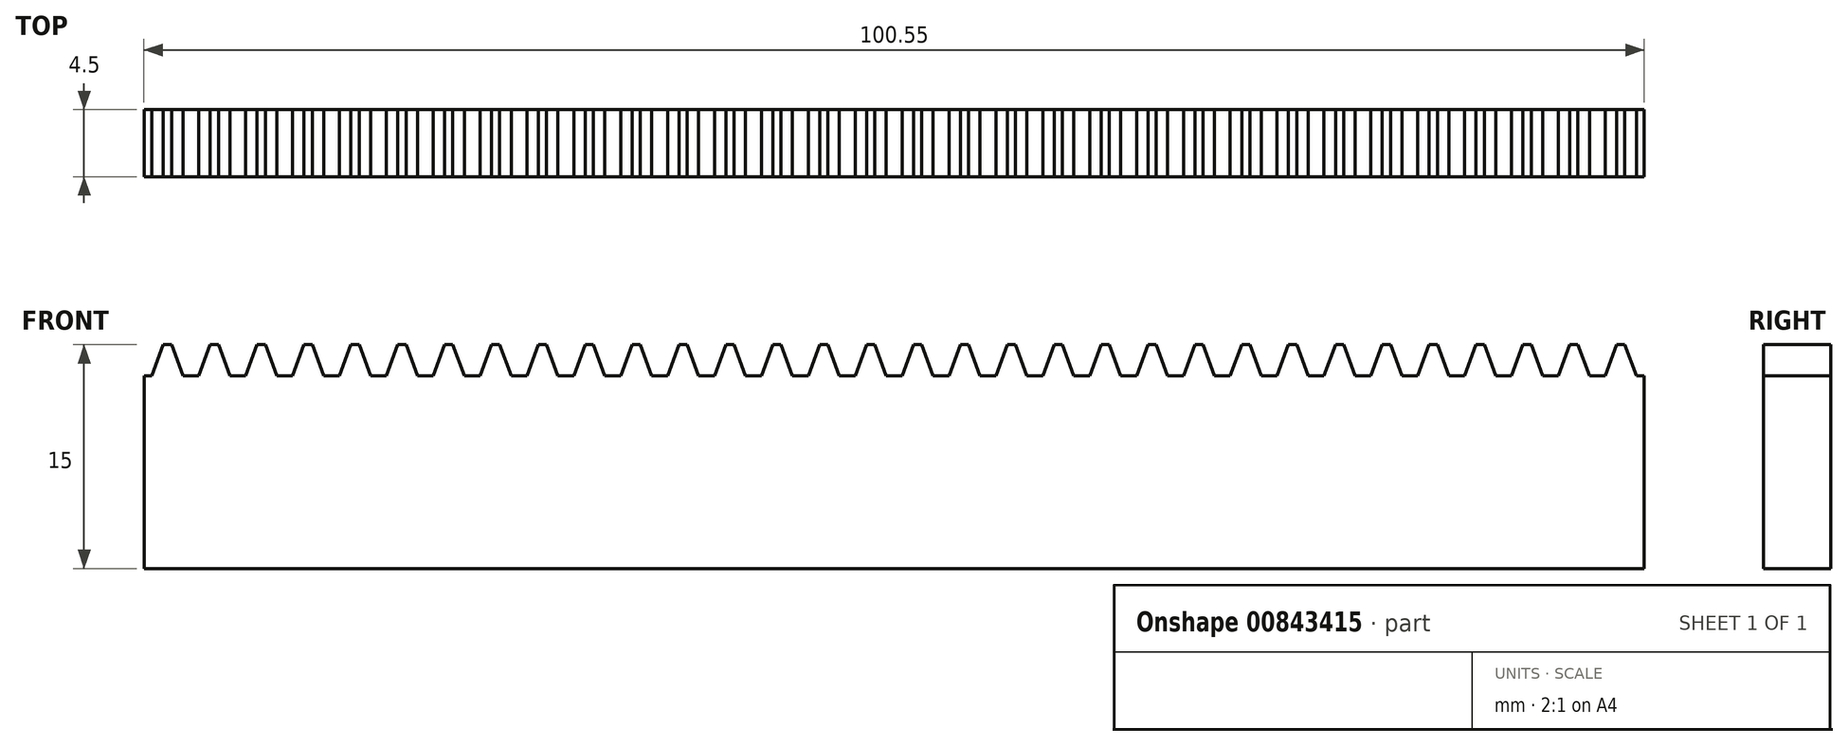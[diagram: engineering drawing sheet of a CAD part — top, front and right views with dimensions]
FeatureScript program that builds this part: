
annotation { "Feature Type Name" : "Feature", "Feature Type Description" : "" }
export const myFeature = defineFeature(function(context is Context, id is Id, definition is map)
    precondition{}
    {
        {
            var Q0;
            Q0=qCreatedBy(makeId("Front.planeOp"),FACE);
            var sketch = newSketch(context, id + "F0", { "sketchPlane" : qUnion([Q0])});
            skLineSegment(sketch, "E0", {"start": v(-394.15, -7.5) * mm, "end": v(-494.7, -7.5) * mm});
            skLineSegment(sketch, "E1", {"start": v(-394.15, 5.4) * mm, "end": v(-394.69, 5.4) * mm});
            skLineSegment(sketch, "E2", {"start": v(-394.69, 5.4) * mm, "end": v(-395.45, 7.5) * mm});
            skLineSegment(sketch, "E3", {"start": v(-396, 7.5) * mm, "end": v(-395.45, 7.5) * mm});
            skLineSegment(sketch, "E4", {"start": v(-396, 7.5) * mm, "end": v(-396.76, 5.4) * mm});
            skLineSegment(sketch, "E5", {"start": v(-396.76, 5.4) * mm, "end": v(-397.83, 5.4) * mm});
            skLineSegment(sketch, "E6", {"start": v(-397.83, 5.4) * mm, "end": v(-398.6, 7.5) * mm});
            skLineSegment(sketch, "E7", {"start": v(-399.14, 7.5) * mm, "end": v(-398.6, 7.5) * mm});
            skLineSegment(sketch, "E8", {"start": v(-399.14, 7.5) * mm, "end": v(-399.9, 5.4) * mm});
            skLineSegment(sketch, "E9", {"start": v(-399.9, 5.4) * mm, "end": v(-400.97, 5.4) * mm});
            skLineSegment(sketch, "E10", {"start": v(-400.97, 5.4) * mm, "end": v(-401.73, 7.5) * mm});
            skLineSegment(sketch, "E11", {"start": v(-402.28, 7.5) * mm, "end": v(-401.73, 7.5) * mm});
            skLineSegment(sketch, "E12", {"start": v(-402.28, 7.5) * mm, "end": v(-403.04, 5.4) * mm});
            skLineSegment(sketch, "E13", {"start": v(-403.04, 5.4) * mm, "end": v(-404.11, 5.4) * mm});
            skLineSegment(sketch, "E14", {"start": v(-404.11, 5.4) * mm, "end": v(-404.88, 7.5) * mm});
            skLineSegment(sketch, "E15", {"start": v(-405.42, 7.5) * mm, "end": v(-404.88, 7.5) * mm});
            skLineSegment(sketch, "E16", {"start": v(-405.42, 7.5) * mm, "end": v(-406.19, 5.4) * mm});
            skLineSegment(sketch, "E17", {"start": v(-406.19, 5.4) * mm, "end": v(-407.25, 5.4) * mm});
            skLineSegment(sketch, "E18", {"start": v(-407.25, 5.4) * mm, "end": v(-408.02, 7.5) * mm});
            skLineSegment(sketch, "E19", {"start": v(-408.56, 7.5) * mm, "end": v(-408.02, 7.5) * mm});
            skLineSegment(sketch, "E20", {"start": v(-408.56, 7.5) * mm, "end": v(-409.33, 5.4) * mm});
            skLineSegment(sketch, "E21", {"start": v(-409.33, 5.4) * mm, "end": v(-410.4, 5.4) * mm});
            skLineSegment(sketch, "E22", {"start": v(-410.4, 5.4) * mm, "end": v(-411.16, 7.5) * mm});
            skLineSegment(sketch, "E23", {"start": v(-411.7, 7.5) * mm, "end": v(-411.16, 7.5) * mm});
            skLineSegment(sketch, "E24", {"start": v(-411.7, 7.5) * mm, "end": v(-412.47, 5.4) * mm});
            skLineSegment(sketch, "E25", {"start": v(-412.47, 5.4) * mm, "end": v(-413.54, 5.4) * mm});
            skLineSegment(sketch, "E26", {"start": v(-413.54, 5.4) * mm, "end": v(-414.3, 7.5) * mm});
            skLineSegment(sketch, "E27", {"start": v(-414.85, 7.5) * mm, "end": v(-414.3, 7.5) * mm});
            skLineSegment(sketch, "E28", {"start": v(-414.85, 7.5) * mm, "end": v(-415.61, 5.4) * mm});
            skLineSegment(sketch, "E29", {"start": v(-415.61, 5.4) * mm, "end": v(-416.68, 5.4) * mm});
            skLineSegment(sketch, "E30", {"start": v(-416.68, 5.4) * mm, "end": v(-417.44, 7.5) * mm});
            skLineSegment(sketch, "E31", {"start": v(-417.99, 7.5) * mm, "end": v(-417.44, 7.5) * mm});
            skLineSegment(sketch, "E32", {"start": v(-417.99, 7.5) * mm, "end": v(-418.75, 5.4) * mm});
            skLineSegment(sketch, "E33", {"start": v(-418.75, 5.4) * mm, "end": v(-419.82, 5.4) * mm});
            skLineSegment(sketch, "E34", {"start": v(-419.82, 5.4) * mm, "end": v(-420.59, 7.5) * mm});
            skLineSegment(sketch, "E35", {"start": v(-421.13, 7.5) * mm, "end": v(-420.59, 7.5) * mm});
            skLineSegment(sketch, "E36", {"start": v(-421.13, 7.5) * mm, "end": v(-421.9, 5.4) * mm});
            skLineSegment(sketch, "E37", {"start": v(-421.9, 5.4) * mm, "end": v(-422.96, 5.4) * mm});
            skLineSegment(sketch, "E38", {"start": v(-422.96, 5.4) * mm, "end": v(-423.73, 7.5) * mm});
            skLineSegment(sketch, "E39", {"start": v(-424.27, 7.5) * mm, "end": v(-423.73, 7.5) * mm});
            skLineSegment(sketch, "E40", {"start": v(-424.27, 7.5) * mm, "end": v(-425.04, 5.4) * mm});
            skLineSegment(sketch, "E41", {"start": v(-425.04, 5.4) * mm, "end": v(-426.1, 5.4) * mm});
            skLineSegment(sketch, "E42", {"start": v(-426.1, 5.4) * mm, "end": v(-426.87, 7.5) * mm});
            skLineSegment(sketch, "E43", {"start": v(-427.42, 7.5) * mm, "end": v(-426.87, 7.5) * mm});
            skLineSegment(sketch, "E44", {"start": v(-427.42, 7.5) * mm, "end": v(-428.18, 5.4) * mm});
            skLineSegment(sketch, "E45", {"start": v(-428.18, 5.4) * mm, "end": v(-429.25, 5.4) * mm});
            skLineSegment(sketch, "E46", {"start": v(-429.25, 5.4) * mm, "end": v(-430.01, 7.5) * mm});
            skLineSegment(sketch, "E47", {"start": v(-430.56, 7.5) * mm, "end": v(-430.01, 7.5) * mm});
            skLineSegment(sketch, "E48", {"start": v(-430.56, 7.5) * mm, "end": v(-431.32, 5.4) * mm});
            skLineSegment(sketch, "E49", {"start": v(-431.32, 5.4) * mm, "end": v(-432.39, 5.4) * mm});
            skLineSegment(sketch, "E50", {"start": v(-432.39, 5.4) * mm, "end": v(-433.15, 7.5) * mm});
            skLineSegment(sketch, "E51", {"start": v(-433.7, 7.5) * mm, "end": v(-433.15, 7.5) * mm});
            skLineSegment(sketch, "E52", {"start": v(-433.7, 7.5) * mm, "end": v(-434.46, 5.4) * mm});
            skLineSegment(sketch, "E53", {"start": v(-434.46, 5.4) * mm, "end": v(-435.53, 5.4) * mm});
            skLineSegment(sketch, "E54", {"start": v(-435.53, 5.4) * mm, "end": v(-436.3, 7.5) * mm});
            skLineSegment(sketch, "E55", {"start": v(-436.84, 7.5) * mm, "end": v(-436.3, 7.5) * mm});
            skLineSegment(sketch, "E56", {"start": v(-436.84, 7.5) * mm, "end": v(-437.6, 5.4) * mm});
            skLineSegment(sketch, "E57", {"start": v(-437.6, 5.4) * mm, "end": v(-438.67, 5.4) * mm});
            skLineSegment(sketch, "E58", {"start": v(-438.67, 5.4) * mm, "end": v(-439.44, 7.5) * mm});
            skLineSegment(sketch, "E59", {"start": v(-439.98, 7.5) * mm, "end": v(-439.44, 7.5) * mm});
            skLineSegment(sketch, "E60", {"start": v(-439.98, 7.5) * mm, "end": v(-440.75, 5.4) * mm});
            skLineSegment(sketch, "E61", {"start": v(-440.75, 5.4) * mm, "end": v(-441.81, 5.4) * mm});
            skLineSegment(sketch, "E62", {"start": v(-441.81, 5.4) * mm, "end": v(-442.58, 7.5) * mm});
            skLineSegment(sketch, "E63", {"start": v(-443.13, 7.5) * mm, "end": v(-442.58, 7.5) * mm});
            skLineSegment(sketch, "E64", {"start": v(-443.13, 7.5) * mm, "end": v(-443.9, 5.4) * mm});
            skLineSegment(sketch, "E65", {"start": v(-443.9, 5.4) * mm, "end": v(-444.96, 5.4) * mm});
            skLineSegment(sketch, "E66", {"start": v(-444.96, 5.4) * mm, "end": v(-445.72, 7.5) * mm});
            skLineSegment(sketch, "E67", {"start": v(-446.27, 7.5) * mm, "end": v(-445.72, 7.5) * mm});
            skLineSegment(sketch, "E68", {"start": v(-446.27, 7.5) * mm, "end": v(-447.03, 5.4) * mm});
            skLineSegment(sketch, "E69", {"start": v(-447.03, 5.4) * mm, "end": v(-448.1, 5.4) * mm});
            skLineSegment(sketch, "E70", {"start": v(-448.1, 5.4) * mm, "end": v(-448.86, 7.5) * mm});
            skLineSegment(sketch, "E71", {"start": v(-449.4, 7.5) * mm, "end": v(-448.86, 7.5) * mm});
            skLineSegment(sketch, "E72", {"start": v(-449.4, 7.5) * mm, "end": v(-450.17, 5.4) * mm});
            skLineSegment(sketch, "E73", {"start": v(-450.17, 5.4) * mm, "end": v(-451.24, 5.4) * mm});
            skLineSegment(sketch, "E74", {"start": v(-451.24, 5.4) * mm, "end": v(-452, 7.5) * mm});
            skLineSegment(sketch, "E75", {"start": v(-452.55, 7.5) * mm, "end": v(-452, 7.5) * mm});
            skLineSegment(sketch, "E76", {"start": v(-452.55, 7.5) * mm, "end": v(-453.32, 5.4) * mm});
            skLineSegment(sketch, "E77", {"start": v(-453.32, 5.4) * mm, "end": v(-454.38, 5.4) * mm});
            skLineSegment(sketch, "E78", {"start": v(-454.38, 5.4) * mm, "end": v(-455.15, 7.5) * mm});
            skLineSegment(sketch, "E79", {"start": v(-455.7, 7.5) * mm, "end": v(-455.15, 7.5) * mm});
            skLineSegment(sketch, "E80", {"start": v(-455.7, 7.5) * mm, "end": v(-456.46, 5.4) * mm});
            skLineSegment(sketch, "E81", {"start": v(-456.46, 5.4) * mm, "end": v(-457.53, 5.4) * mm});
            skLineSegment(sketch, "E82", {"start": v(-457.53, 5.4) * mm, "end": v(-458.29, 7.5) * mm});
            skLineSegment(sketch, "E83", {"start": v(-458.84, 7.5) * mm, "end": v(-458.29, 7.5) * mm});
            skLineSegment(sketch, "E84", {"start": v(-458.84, 7.5) * mm, "end": v(-459.6, 5.4) * mm});
            skLineSegment(sketch, "E85", {"start": v(-459.6, 5.4) * mm, "end": v(-460.67, 5.4) * mm});
            skLineSegment(sketch, "E86", {"start": v(-460.67, 5.4) * mm, "end": v(-461.43, 7.5) * mm});
            skLineSegment(sketch, "E87", {"start": v(-461.98, 7.5) * mm, "end": v(-461.43, 7.5) * mm});
            skLineSegment(sketch, "E88", {"start": v(-461.98, 7.5) * mm, "end": v(-462.74, 5.4) * mm});
            skLineSegment(sketch, "E89", {"start": v(-462.74, 5.4) * mm, "end": v(-463.8, 5.4) * mm});
            skLineSegment(sketch, "E90", {"start": v(-463.8, 5.4) * mm, "end": v(-464.57, 7.5) * mm});
            skLineSegment(sketch, "E91", {"start": v(-465.12, 7.5) * mm, "end": v(-464.57, 7.5) * mm});
            skLineSegment(sketch, "E92", {"start": v(-465.12, 7.5) * mm, "end": v(-465.88, 5.4) * mm});
            skLineSegment(sketch, "E93", {"start": v(-465.88, 5.4) * mm, "end": v(-466.95, 5.4) * mm});
            skLineSegment(sketch, "E94", {"start": v(-466.95, 5.4) * mm, "end": v(-467.72, 7.5) * mm});
            skLineSegment(sketch, "E95", {"start": v(-468.26, 7.5) * mm, "end": v(-467.72, 7.5) * mm});
            skLineSegment(sketch, "E96", {"start": v(-468.26, 7.5) * mm, "end": v(-469.03, 5.4) * mm});
            skLineSegment(sketch, "E97", {"start": v(-469.03, 5.4) * mm, "end": v(-470.1, 5.4) * mm});
            skLineSegment(sketch, "E98", {"start": v(-470.1, 5.4) * mm, "end": v(-470.86, 7.5) * mm});
            skLineSegment(sketch, "E99", {"start": v(-471.4, 7.5) * mm, "end": v(-470.86, 7.5) * mm});
            skLineSegment(sketch, "E100", {"start": v(-471.4, 7.5) * mm, "end": v(-472.17, 5.4) * mm});
            skLineSegment(sketch, "E101", {"start": v(-472.17, 5.4) * mm, "end": v(-473.24, 5.4) * mm});
            skLineSegment(sketch, "E102", {"start": v(-473.24, 5.4) * mm, "end": v(-474, 7.5) * mm});
            skLineSegment(sketch, "E103", {"start": v(-474.55, 7.5) * mm, "end": v(-474, 7.5) * mm});
            skLineSegment(sketch, "E104", {"start": v(-474.55, 7.5) * mm, "end": v(-475.3, 5.4) * mm});
            skLineSegment(sketch, "E105", {"start": v(-475.3, 5.4) * mm, "end": v(-476.38, 5.4) * mm});
            skLineSegment(sketch, "E106", {"start": v(-476.38, 5.4) * mm, "end": v(-477.14, 7.5) * mm});
            skLineSegment(sketch, "E107", {"start": v(-477.69, 7.5) * mm, "end": v(-477.14, 7.5) * mm});
            skLineSegment(sketch, "E108", {"start": v(-477.69, 7.5) * mm, "end": v(-478.45, 5.4) * mm});
            skLineSegment(sketch, "E109", {"start": v(-478.45, 5.4) * mm, "end": v(-479.52, 5.4) * mm});
            skLineSegment(sketch, "E110", {"start": v(-479.52, 5.4) * mm, "end": v(-480.28, 7.5) * mm});
            skLineSegment(sketch, "E111", {"start": v(-480.83, 7.5) * mm, "end": v(-480.28, 7.5) * mm});
            skLineSegment(sketch, "E112", {"start": v(-480.83, 7.5) * mm, "end": v(-481.6, 5.4) * mm});
            skLineSegment(sketch, "E113", {"start": v(-481.6, 5.4) * mm, "end": v(-482.66, 5.4) * mm});
            skLineSegment(sketch, "E114", {"start": v(-482.66, 5.4) * mm, "end": v(-483.43, 7.5) * mm});
            skLineSegment(sketch, "E115", {"start": v(-483.97, 7.5) * mm, "end": v(-483.43, 7.5) * mm});
            skLineSegment(sketch, "E116", {"start": v(-483.97, 7.5) * mm, "end": v(-484.74, 5.4) * mm});
            skLineSegment(sketch, "E117", {"start": v(-484.74, 5.4) * mm, "end": v(-485.8, 5.4) * mm});
            skLineSegment(sketch, "E118", {"start": v(-485.8, 5.4) * mm, "end": v(-486.57, 7.5) * mm});
            skLineSegment(sketch, "E119", {"start": v(-487.11, 7.5) * mm, "end": v(-486.57, 7.5) * mm});
            skLineSegment(sketch, "E120", {"start": v(-487.11, 7.5) * mm, "end": v(-487.88, 5.4) * mm});
            skLineSegment(sketch, "E121", {"start": v(-487.88, 5.4) * mm, "end": v(-488.94, 5.4) * mm});
            skLineSegment(sketch, "E122", {"start": v(-488.94, 5.4) * mm, "end": v(-489.7, 7.5) * mm});
            skLineSegment(sketch, "E123", {"start": v(-490.26, 7.5) * mm, "end": v(-489.7, 7.5) * mm});
            skLineSegment(sketch, "E124", {"start": v(-490.26, 7.5) * mm, "end": v(-491.02, 5.4) * mm});
            skLineSegment(sketch, "E125", {"start": v(-491.02, 5.4) * mm, "end": v(-492.09, 5.4) * mm});
            skLineSegment(sketch, "E126", {"start": v(-492.09, 5.4) * mm, "end": v(-492.85, 7.5) * mm});
            skLineSegment(sketch, "E127", {"start": v(-493.4, 7.5) * mm, "end": v(-492.85, 7.5) * mm});
            skLineSegment(sketch, "E128", {"start": v(-493.4, 7.5) * mm, "end": v(-494.16, 5.4) * mm});
            skLineSegment(sketch, "E129", {"start": v(-494.16, 5.4) * mm, "end": v(-494.7, 5.4) * mm});
            skLineSegment(sketch, "E130", {"start": v(-494.7, 5.4) * mm, "end": v(-494.7, -7.5) * mm});
            skLineSegment(sketch, "E131", {"start": v(-394.15, 5.4) * mm, "end": v(-394.15, -7.5) * mm});
            skSolve(sketch);
        }
        {
            var Q0;
            Q0 = qSketchRegion(id + "F0", true);
            extrude(context, id + "F1", {"entities" : qUnion([Q0]), "depth" : 4.5 * mm, "offsetDistance" : 25 * mm});
        }
    });
